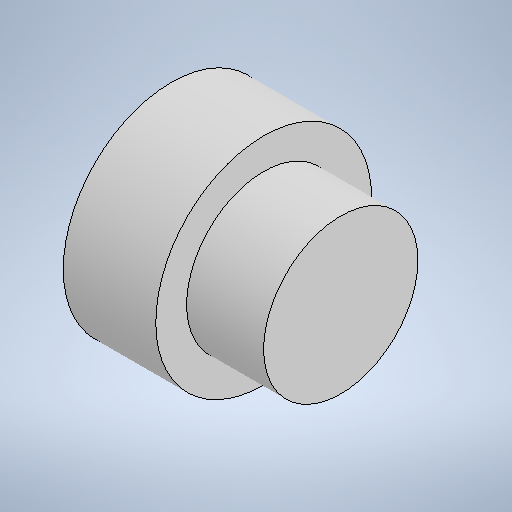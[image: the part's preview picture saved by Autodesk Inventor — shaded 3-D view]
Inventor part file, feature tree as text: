
AUTODESK INVENTOR PART (.ipt)
format: ipt  version: 2025 (Build 290162010, 162A)  size: 231,424 bytes
history: native  units: mm
features: sketch x2, revolve x1, hole x1
ambient origin geometry x8: Origin, YZ Plane, XZ Plane, XY Plane, X Axis, Y Axis, Z Axis, Center Point
bodies: Solid1 (feature_tree)
feature tree (4):
  revolve  "Revolution1"  [1 undecoded]
  hole  "Hole1"  [1 undecoded]
  sketch  "Sketch1"  dims[d0=5.0mm d1=6.0mm]
  sketch  "Sketch2"  dims[d2=10.0mm d3=14.0mm d4=90.0deg d5=4.134mm d6=9.0mm d7=4.0mm d8=2.0mm d9=90.0deg d10=9.0mm d11=0.0mm]
note: 2 required parameter values undecoded (feature->parameter linkage not recoverable at this tier; creation-order binding heuristic only, values carry confidence <= 0.55)